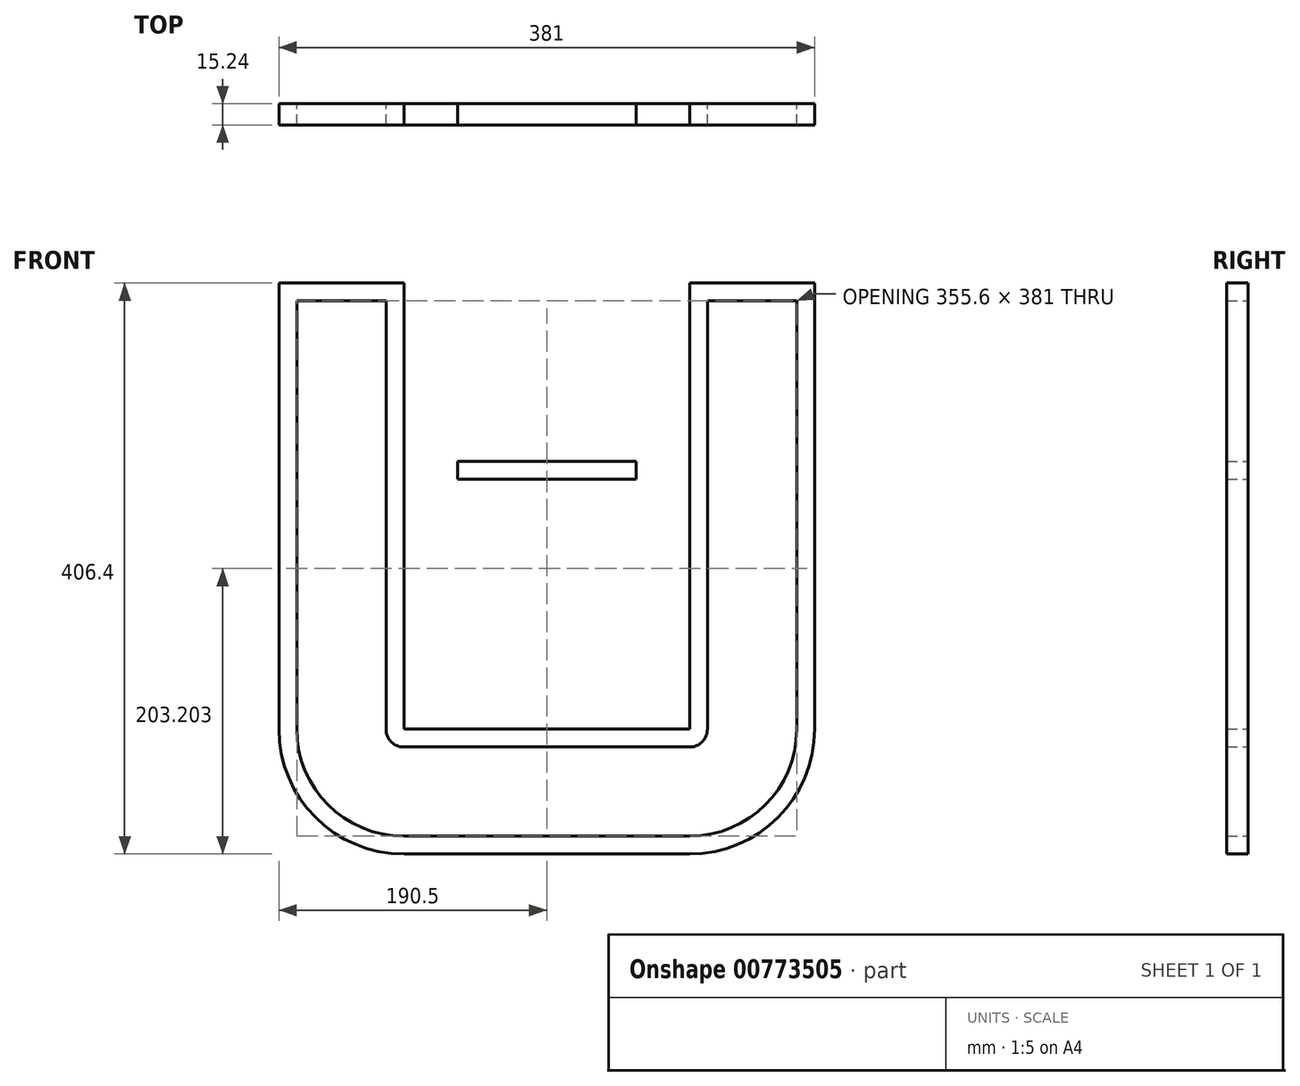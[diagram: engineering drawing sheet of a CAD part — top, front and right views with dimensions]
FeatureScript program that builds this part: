
annotation { "Feature Type Name" : "Feature", "Feature Type Description" : "" }
export const myFeature = defineFeature(function(context is Context, id is Id, definition is map)
    precondition{}
    {
        {
            var Q0;
            Q0=qCreatedBy(makeId("Front.planeOp"),FACE);
            var sketch = newSketch(context, id + "F0", { "sketchPlane" : qUnion([Q0])});
            skLineSegment(sketch, "E0.bottom", {"start": v(-101.6, -191.54) * mm, "end": v(101.6, -191.54) * mm});
            skLineSegment(sketch, "E0.top", {"start": v(-101.6, -204.24) * mm, "end": v(101.6, -204.24) * mm});
            skLineSegment(sketch, "E0.left", {"start": v(-101.6, -191.54) * mm, "end": v(-101.6, -204.24) * mm});
            skLineSegment(sketch, "E0.right", {"start": v(101.6, -191.54) * mm, "end": v(101.6, -204.24) * mm});
            skPoint(sketch, "E1", {"position": v(0, -191.54) * mm});
            skLineSegment(sketch, "E2.bottom", {"start": v(-101.6, -115.34) * mm, "end": v(101.6, -115.34) * mm});
            skLineSegment(sketch, "E2.top", {"start": v(-101.6, -128.04) * mm, "end": v(101.6, -128.04) * mm});
            skLineSegment(sketch, "E2.left", {"start": v(-101.6, -115.34) * mm, "end": v(-101.6, -128.04) * mm});
            skLineSegment(sketch, "E2.right", {"start": v(101.6, -115.34) * mm, "end": v(101.6, -128.04) * mm});
            skPoint(sketch, "E3", {"position": v(0, -115.34) * mm});
            skArc(sketch, "E4", {"start": v(-101.6, -128.04) * mm, "mid": v(-110.58, -124.32) * mm, "end": v(-114.3, -115.34) * mm});
            skArc(sketch, "E5", {"start": v(-101.6, -204.24) * mm, "mid": v(-164.46, -178.2) * mm, "end": v(-190.5, -115.34) * mm});
            skArc(sketch, "E6", {"start": v(-101.6, -191.54) * mm, "mid": v(-155.48, -169.22) * mm, "end": v(-177.8, -115.34) * mm});
            skArc(sketch, "E7", {"start": v(101.6, -128.04) * mm, "mid": v(110.58, -124.32) * mm, "end": v(114.3, -115.34) * mm});
            skArc(sketch, "E8", {"start": v(101.6, -191.54) * mm, "mid": v(155.48, -169.22) * mm, "end": v(177.8, -115.34) * mm});
            skArc(sketch, "E9", {"start": v(101.6, -204.24) * mm, "mid": v(164.46, -178.2) * mm, "end": v(190.5, -115.34) * mm});
            skLineSegment(sketch, "E10.bottom", {"start": v(-190.5, -115.34) * mm, "end": v(-177.8, -115.34) * mm});
            skLineSegment(sketch, "E10.top", {"start": v(-190.5, 189.46) * mm, "end": v(-177.8, 189.46) * mm});
            skLineSegment(sketch, "E10.left", {"start": v(-190.5, -115.34) * mm, "end": v(-190.5, 189.46) * mm});
            skLineSegment(sketch, "E10.right", {"start": v(-177.8, -115.34) * mm, "end": v(-177.8, 189.46) * mm});
            skLineSegment(sketch, "E11.bottom", {"start": v(-114.3, -115.34) * mm, "end": v(-101.6, -115.34) * mm});
            skLineSegment(sketch, "E11.top", {"start": v(-114.3, 189.46) * mm, "end": v(-101.6, 189.46) * mm});
            skLineSegment(sketch, "E11.left", {"start": v(-114.3, -115.34) * mm, "end": v(-114.3, 189.46) * mm});
            skLineSegment(sketch, "E11.right", {"start": v(-101.6, -115.34) * mm, "end": v(-101.6, 189.46) * mm});
            skLineSegment(sketch, "E12.bottom", {"start": v(101.6, -115.34) * mm, "end": v(114.3, -115.34) * mm});
            skLineSegment(sketch, "E12.top", {"start": v(101.6, 189.46) * mm, "end": v(114.3, 189.46) * mm});
            skLineSegment(sketch, "E12.left", {"start": v(101.6, -115.34) * mm, "end": v(101.6, 189.46) * mm});
            skLineSegment(sketch, "E12.right", {"start": v(114.3, -115.34) * mm, "end": v(114.3, 189.46) * mm});
            skLineSegment(sketch, "E13.bottom", {"start": v(177.8, -115.34) * mm, "end": v(190.5, -115.34) * mm});
            skLineSegment(sketch, "E13.top", {"start": v(177.8, 189.46) * mm, "end": v(190.5, 189.46) * mm});
            skLineSegment(sketch, "E13.left", {"start": v(177.8, -115.34) * mm, "end": v(177.8, 189.46) * mm});
            skLineSegment(sketch, "E13.right", {"start": v(190.5, -115.34) * mm, "end": v(190.5, 189.46) * mm});
            skLineSegment(sketch, "E14.bottom", {"start": v(-190.5, 189.46) * mm, "end": v(-101.6, 189.46) * mm});
            skLineSegment(sketch, "E14.top", {"start": v(-190.5, 202.16) * mm, "end": v(-101.6, 202.16) * mm});
            skLineSegment(sketch, "E14.left", {"start": v(-190.5, 189.46) * mm, "end": v(-190.5, 202.16) * mm});
            skLineSegment(sketch, "E14.right", {"start": v(-101.6, 189.46) * mm, "end": v(-101.6, 202.16) * mm});
            skLineSegment(sketch, "E15.bottom", {"start": v(101.6, 189.46) * mm, "end": v(190.5, 189.46) * mm});
            skLineSegment(sketch, "E15.top", {"start": v(101.6, 202.16) * mm, "end": v(190.5, 202.16) * mm});
            skLineSegment(sketch, "E15.left", {"start": v(101.6, 189.46) * mm, "end": v(101.6, 202.16) * mm});
            skLineSegment(sketch, "E15.right", {"start": v(190.5, 189.46) * mm, "end": v(190.5, 202.16) * mm});
            skLineSegment(sketch, "E16.bottom", {"start": v(63.5, 62.46) * mm, "end": v(-63.5, 62.46) * mm});
            skLineSegment(sketch, "E16.top", {"start": v(63.5, 75.16) * mm, "end": v(-63.5, 75.16) * mm});
            skLineSegment(sketch, "E16.left", {"start": v(63.5, 62.46) * mm, "end": v(63.5, 75.16) * mm});
            skLineSegment(sketch, "E16.right", {"start": v(-63.5, 62.46) * mm, "end": v(-63.5, 75.16) * mm});
            skPoint(sketch, "E16.middle", {"position": v(0, 68.81) * mm});
            skSolve(sketch);
        }
        {
            var Q0;
            Q0 = qSketchRegion(id + "F0", true);
            extrude(context, id + "F1", {"entities" : qUnion([Q0]), "depth" : 15.24 * mm, "offsetDistance" : 25.4 * mm});
        }
    });
